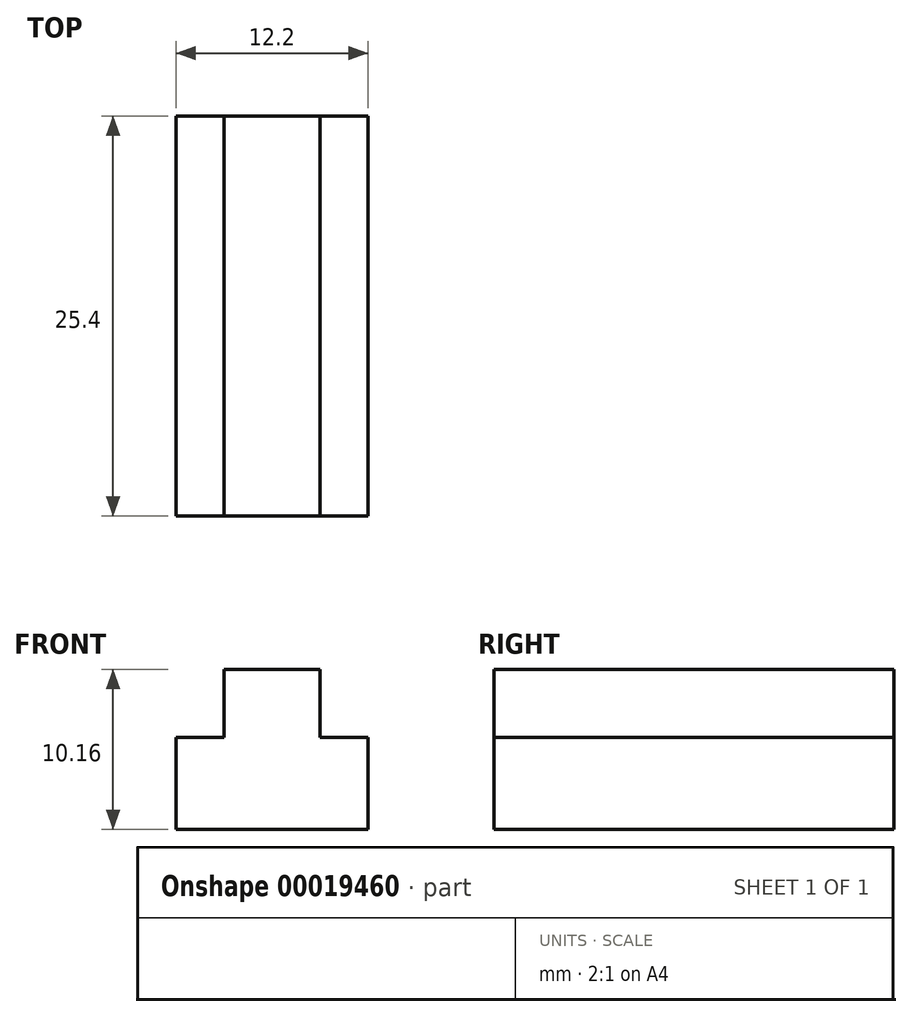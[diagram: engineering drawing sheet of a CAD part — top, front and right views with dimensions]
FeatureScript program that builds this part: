
annotation { "Feature Type Name" : "Feature", "Feature Type Description" : "" }
export const myFeature = defineFeature(function(context is Context, id is Id, definition is map)
    precondition{}
    {
        {
            var Q0;
            Q0=qCreatedBy(makeId("Front.planeOp"),FACE);
            var sketch = newSketch(context, id + "F0", { "sketchPlane" : qUnion([Q0])});
            skLineSegment(sketch, "E0", {"start": v(0, 6.43) * mm, "end": v(0, -5.66) * mm, "construction": true});
            skLineSegment(sketch, "E1", {"start": v(0, 4.32) * mm, "end": v(3.05, 4.32) * mm});
            skLineSegment(sketch, "E2", {"start": v(3.05, 4.32) * mm, "end": v(3.05, 0) * mm});
            skLineSegment(sketch, "E3", {"start": v(3.05, 0) * mm, "end": v(6.1, 0) * mm});
            skLineSegment(sketch, "E4", {"start": v(6.1, 0) * mm, "end": v(6.1, -5.84) * mm});
            skLineSegment(sketch, "E5", {"start": v(6.1, -5.84) * mm, "end": v(0, -5.84) * mm});
            skLineSegment(sketch, "E6.MirrorCS", {"start": v(-3.05, 0) * mm, "end": v(-6.1, 0) * mm});
            skLineSegment(sketch, "E7.MirrorCS", {"start": v(-6.1, 0) * mm, "end": v(-6.1, -5.84) * mm});
            skLineSegment(sketch, "E8.MirrorCS", {"start": v(-6.1, -5.84) * mm, "end": v(0, -5.84) * mm});
            skLineSegment(sketch, "E9.MirrorCS", {"start": v(0, 4.32) * mm, "end": v(-3.05, 4.32) * mm});
            skLineSegment(sketch, "E10.MirrorCS", {"start": v(-3.05, 4.32) * mm, "end": v(-3.05, 0) * mm});
            skSolve(sketch);
        }
        {
            var Q0;
            Q0 = qSketchRegion(id + "F0", true);
            extrude(context, id + "F1", {"entities" : qUnion([Q0]), "endBound" : BoundingType.SYMMETRIC, "depth" : 25.4 * mm});
        }
    });
